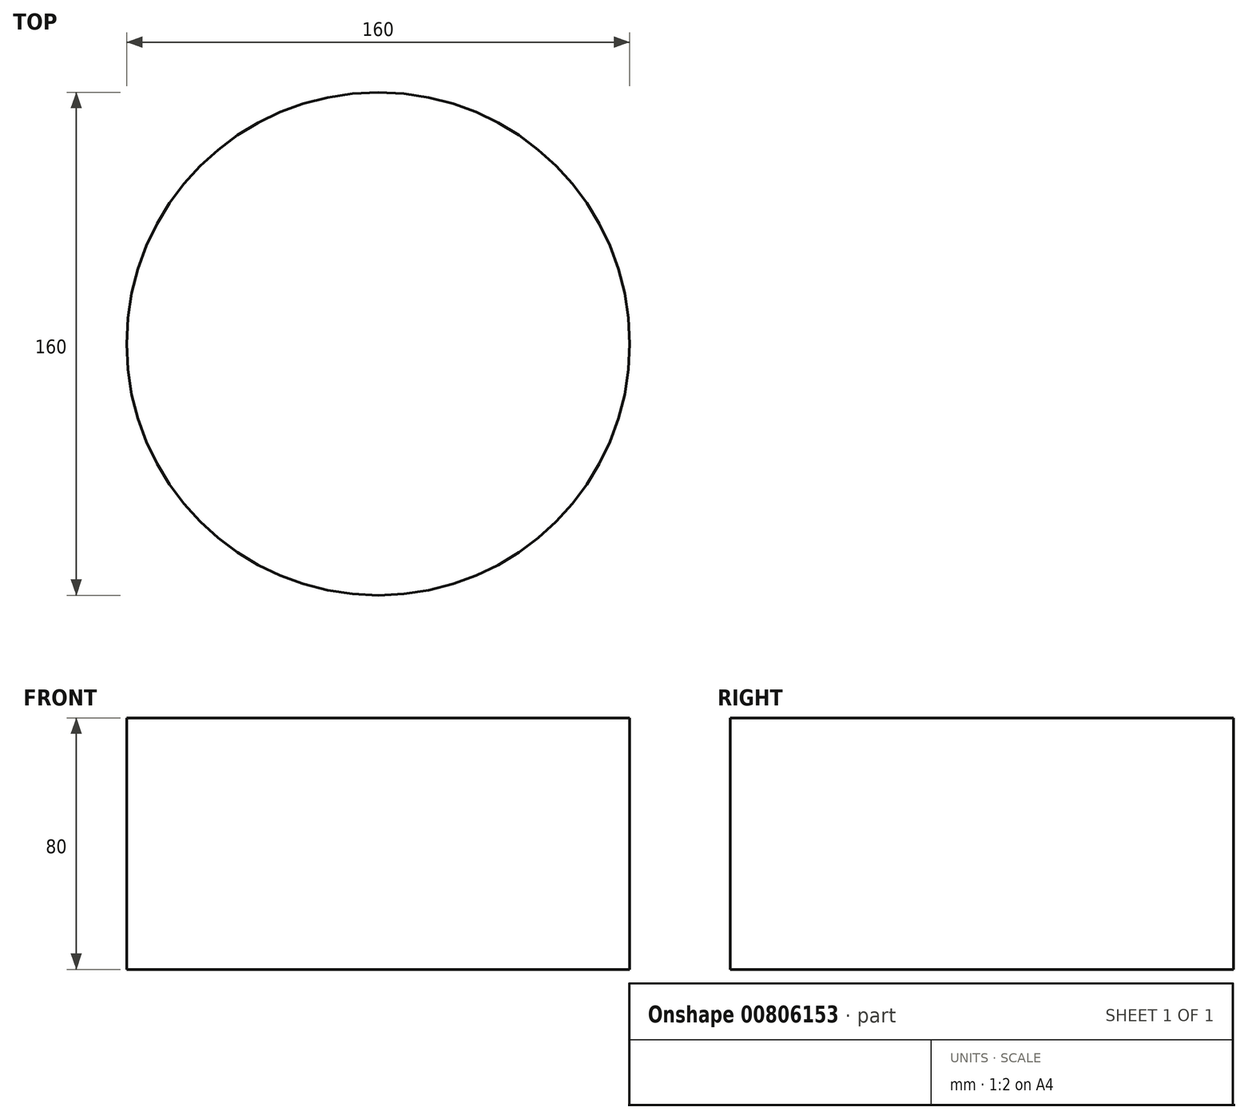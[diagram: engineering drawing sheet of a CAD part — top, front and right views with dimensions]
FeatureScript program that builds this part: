
annotation { "Feature Type Name" : "Feature", "Feature Type Description" : "" }
export const myFeature = defineFeature(function(context is Context, id is Id, definition is map)
    precondition{}
    {
        {
            var Q0;
            Q0=qCreatedBy(makeId("Top.planeOp"),FACE);
            var sketch = newSketch(context, id + "F0", { "sketchPlane" : qUnion([Q0])});
            skCircle(sketch, "E0", {"center": v(0, 0) * mm, "radius": 80 * mm});
            skSolve(sketch);
        }
        {
            var Q0;
            Q0=qSketchRegion(id+"F0",true);
            extrude(context, id + "F1", {"entities" : qUnion([Q0]), "depth" : 80 * mm, "offsetDistance" : 25 * mm});
        }
    });
